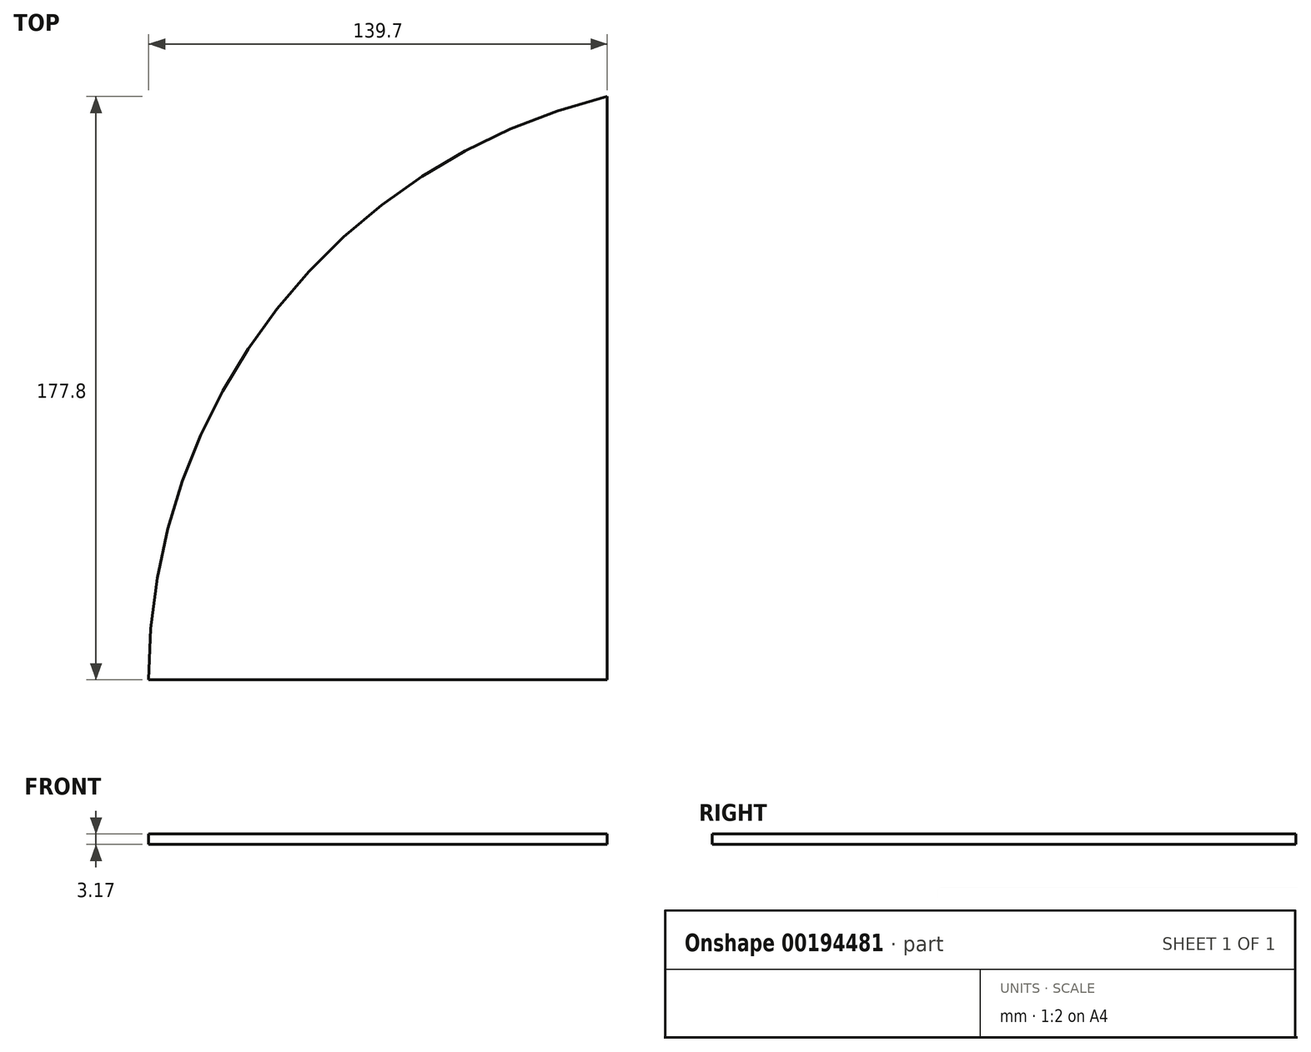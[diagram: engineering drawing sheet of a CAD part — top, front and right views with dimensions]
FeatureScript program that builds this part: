
annotation { "Feature Type Name" : "Feature", "Feature Type Description" : "" }
export const myFeature = defineFeature(function(context is Context, id is Id, definition is map)
    precondition{}
    {
        {
            var Q0;
            Q0=qCreatedBy(makeId("Top.planeOp"),FACE);
            var sketch = newSketch(context, id + "F0", { "sketchPlane" : qUnion([Q0])});
            skLineSegment(sketch, "E0", {"start": v(0, 0) * mm, "end": v(-139.7, 0) * mm});
            skLineSegment(sketch, "E1", {"start": v(0, 0) * mm, "end": v(0, 177.8) * mm});
            skArc(sketch, "E2.0", {"start": v(0, 177.8) * mm, "mid": v(-100.6, 113.06) * mm, "end": v(-139.7, 0) * mm});
            skPoint(sketch, "E3.orphan", {"position": v(0, 177.8) * mm});
            skSolve(sketch);
        }
        {
            var Q0;
            Q0=makeQuery(id+"F0.imprint","IMPRINT",FACE,{"disambiguationData":[TD([[makeQuery(id+"F0.imprint","IMPRINT",EDGE,{"derivedFrom":sQuery(id+"F0.wireOp",EDGE,"E0")}),-1.0]])]});
            extrude(context, id + "F1", {"entities" : qUnion([Q0]), "depth" : 3.17 * mm});
        }
    });
